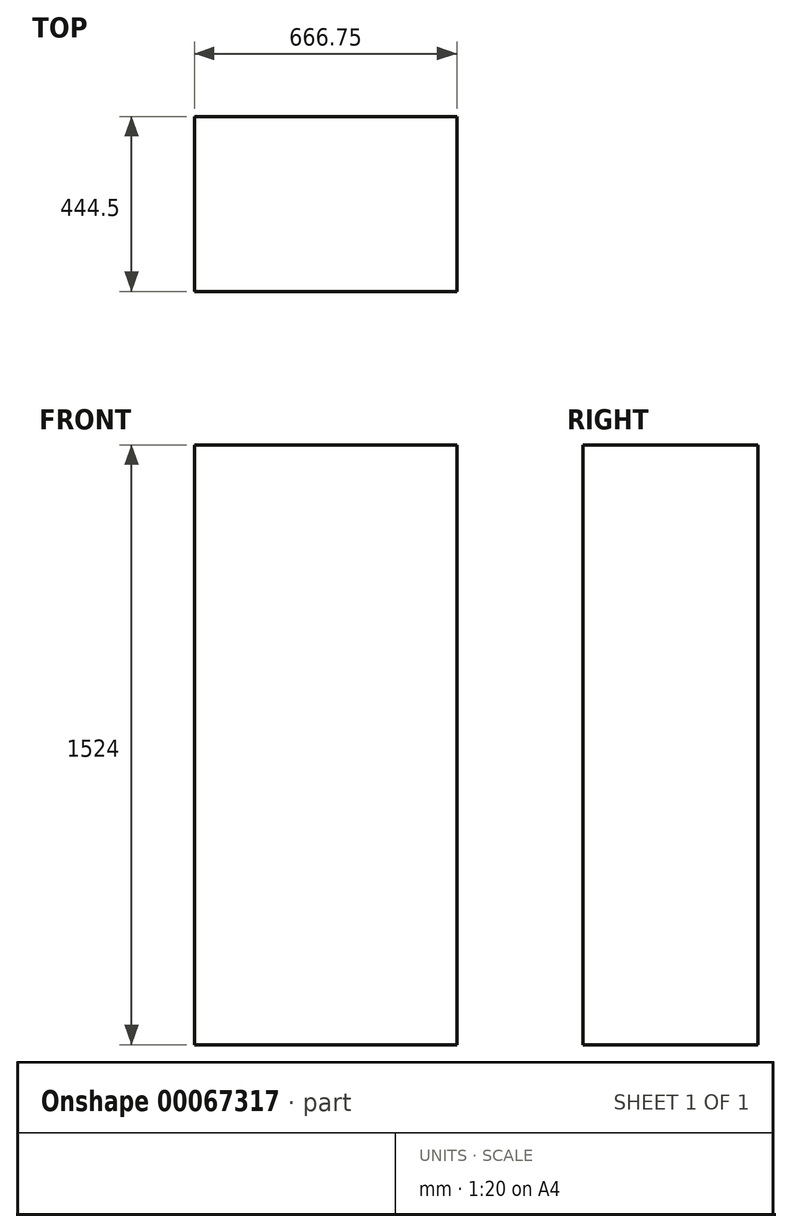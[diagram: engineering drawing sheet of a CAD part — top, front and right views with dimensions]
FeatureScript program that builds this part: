
annotation { "Feature Type Name" : "Feature", "Feature Type Description" : "" }
export const myFeature = defineFeature(function(context is Context, id is Id, definition is map)
    precondition{}
    {
        {
            var Q0;
            Q0=qCreatedBy(makeId("Top.planeOp"),FACE);
            var sketch = newSketch(context, id + "F0", { "sketchPlane" : qUnion([Q0])});
            skLineSegment(sketch, "E0.bottom", {"start": v(-302.65, 280.82) * mm, "end": v(364.1, 280.82) * mm});
            skLineSegment(sketch, "E0.top", {"start": v(-302.65, -163.68) * mm, "end": v(364.1, -163.68) * mm});
            skLineSegment(sketch, "E0.left", {"start": v(-302.65, 280.82) * mm, "end": v(-302.65, -163.68) * mm});
            skLineSegment(sketch, "E0.right", {"start": v(364.1, 280.82) * mm, "end": v(364.1, -163.68) * mm});
            skSolve(sketch);
        }
        {
            var Q0;
            Q0 = qSketchRegion(id + "F0", true);
            extrude(context, id + "F1", {"entities" : qUnion([Q0]), "depth" : 1524 * mm});
        }
    });
